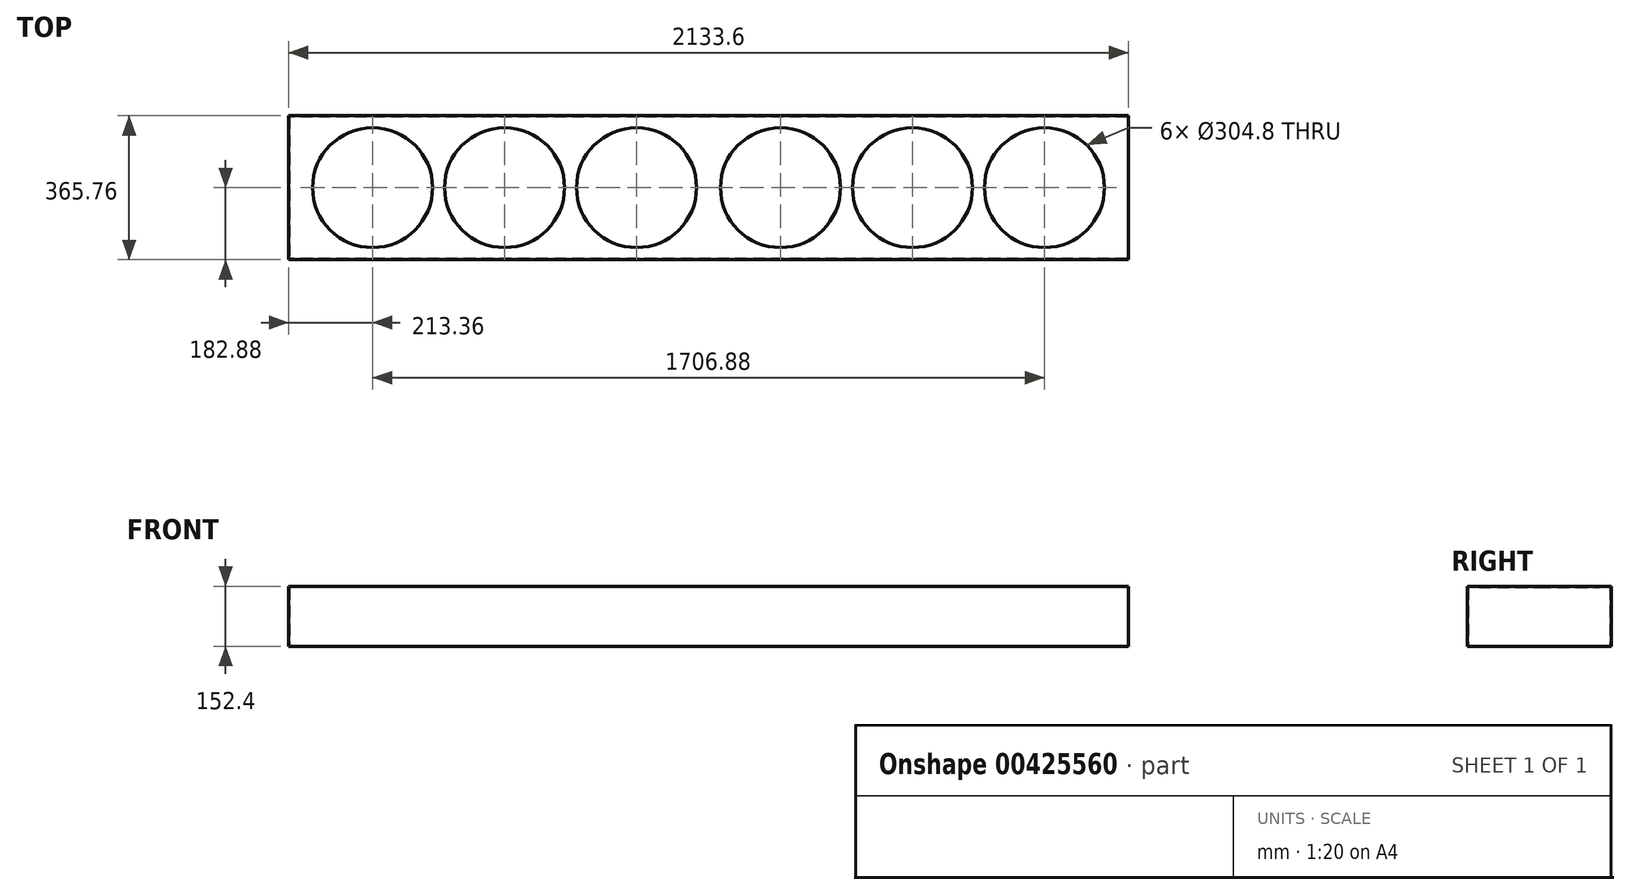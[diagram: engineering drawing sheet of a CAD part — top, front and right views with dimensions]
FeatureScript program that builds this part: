
annotation { "Feature Type Name" : "Feature", "Feature Type Description" : "" }
export const myFeature = defineFeature(function(context is Context, id is Id, definition is map)
    precondition{}
    {
        {
            var Q0;
            Q0=qCreatedBy(makeId("Top.planeOp"),FACE);
            var sketch = newSketch(context, id + "F0", { "sketchPlane" : qUnion([Q0])});
            skLineSegment(sketch, "E0.bottom", {"start": v(1066.8, 182.88) * mm, "end": v(-1066.8, 182.88) * mm});
            skLineSegment(sketch, "E0.top", {"start": v(1066.8, -182.88) * mm, "end": v(-1066.8, -182.88) * mm});
            skLineSegment(sketch, "E0.left", {"start": v(1066.8, 182.88) * mm, "end": v(1066.8, -182.88) * mm});
            skLineSegment(sketch, "E0.right", {"start": v(-1066.8, 182.88) * mm, "end": v(-1066.8, -182.88) * mm});
            skPoint(sketch, "E0.middle", {"position": v(0, 0) * mm});
            skSolve(sketch);
        }
        {
            var Q0;
            Q0 = qSketchRegion(id + "F0", true);
            extrude(context, id + "F1", {"entities" : qUnion([Q0]), "depth" : 152.4 * mm});
        }
        {
            var Q0;
            Q0=makeQuery(id+"F1.opExtrude","CAP_FACE",FACE,{"disambiguationData":[OSD([sQuery(id+"F0.wireOp",EDGE,"E0.bottom"),sQuery(id+"F0.wireOp",EDGE,"E0.top"),sQuery(id+"F0.wireOp",EDGE,"E0.left"),sQuery(id+"F0.wireOp",EDGE,"E0.right")])],"isStart":true});
            shell(context, id + "F2", {"entities" : qUnion([Q0]), "thickness" : 3.05 * mm});
        }
        {
            var Q0;
            Q0=makeQuery(id+"F1.opExtrude","CAP_FACE",FACE,{"disambiguationData":[OSD([sQuery(id+"F0.wireOp",EDGE,"E0.bottom"),sQuery(id+"F0.wireOp",EDGE,"E0.top"),sQuery(id+"F0.wireOp",EDGE,"E0.left"),sQuery(id+"F0.wireOp",EDGE,"E0.right")])],"isStart":false});
            var sketch = newSketch(context, id + "F3", { "sketchPlane" : qUnion([Q0])});
            skCircle(sketch, "E1", {"center": v(182.88, 0) * mm, "radius": 152.4 * mm});
            skCircle(sketch, "E2.1.0.0", {"center": v(518.16, 0) * mm, "radius": 152.4 * mm});
            skCircle(sketch, "E2.2.0.0", {"center": v(853.44, 0) * mm, "radius": 152.4 * mm});
            skLineSegment(sketch, "E2.direction1", {"start": v(182.88, 0) * mm, "end": v(518.16, 0) * mm, "construction": true});
            skCircle(sketch, "E3", {"center": v(-182.88, 0) * mm, "radius": 152.4 * mm});
            skCircle(sketch, "E4.1.0.0", {"center": v(-518.16, 0) * mm, "radius": 152.4 * mm});
            skCircle(sketch, "E4.2.0.0", {"center": v(-853.44, 0) * mm, "radius": 152.4 * mm});
            skLineSegment(sketch, "E4.direction1", {"start": v(-182.88, 0) * mm, "end": v(-518.16, 0) * mm, "construction": true});
            skSolve(sketch);
        }
        {
            var Q0;
            Q0 = qSketchRegion(id + "F3", true);
            extrude(context, id + "F4", {"entities" : qUnion([Q0]), "operationType" : NewBodyOperationType.REMOVE, "endBound" : BoundingType.THROUGH_ALL, "oppositeDirection" : true, "depth" : 30.48 * mm});
        }
    });
